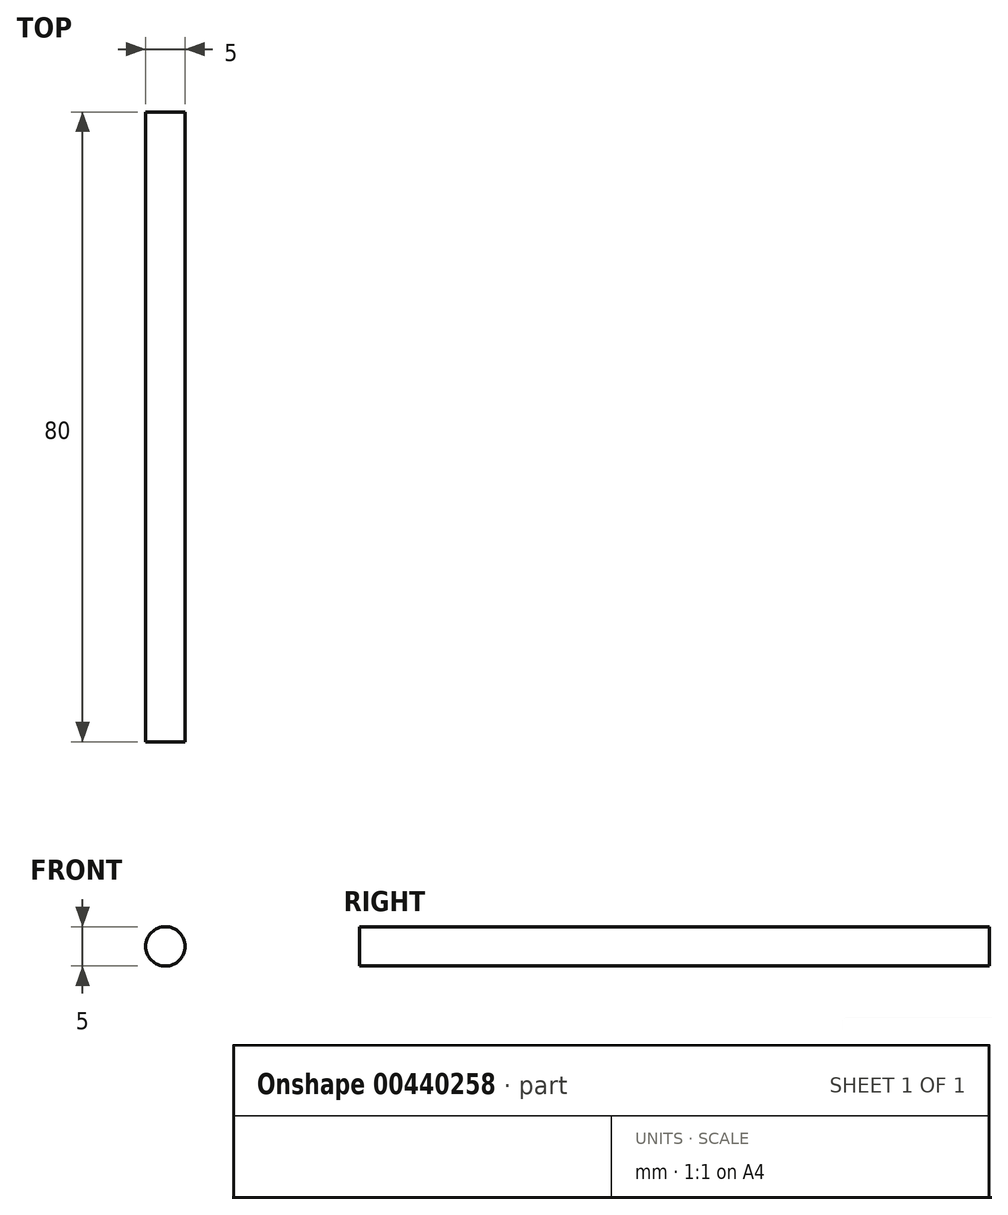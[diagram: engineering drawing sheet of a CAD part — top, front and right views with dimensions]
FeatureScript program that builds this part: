
annotation { "Feature Type Name" : "Feature", "Feature Type Description" : "" }
export const myFeature = defineFeature(function(context is Context, id is Id, definition is map)
    precondition{}
    {
        {
            var Q0;
            Q0=qCreatedBy(makeId("Front.planeOp"),FACE);
            var sketch = newSketch(context, id + "F0", { "sketchPlane" : qUnion([Q0])});
            skCircle(sketch, "E0", {"center": v(0, 0) * mm, "radius": 2.5 * mm});
            skSolve(sketch);
        }
        {
            var Q0;
            Q0 = qSketchRegion(id + "F0", true);
            extrude(context, id + "F1", {"entities" : qUnion([Q0]), "endBound" : BoundingType.SYMMETRIC, "depth" : 80 * mm});
        }
    });
